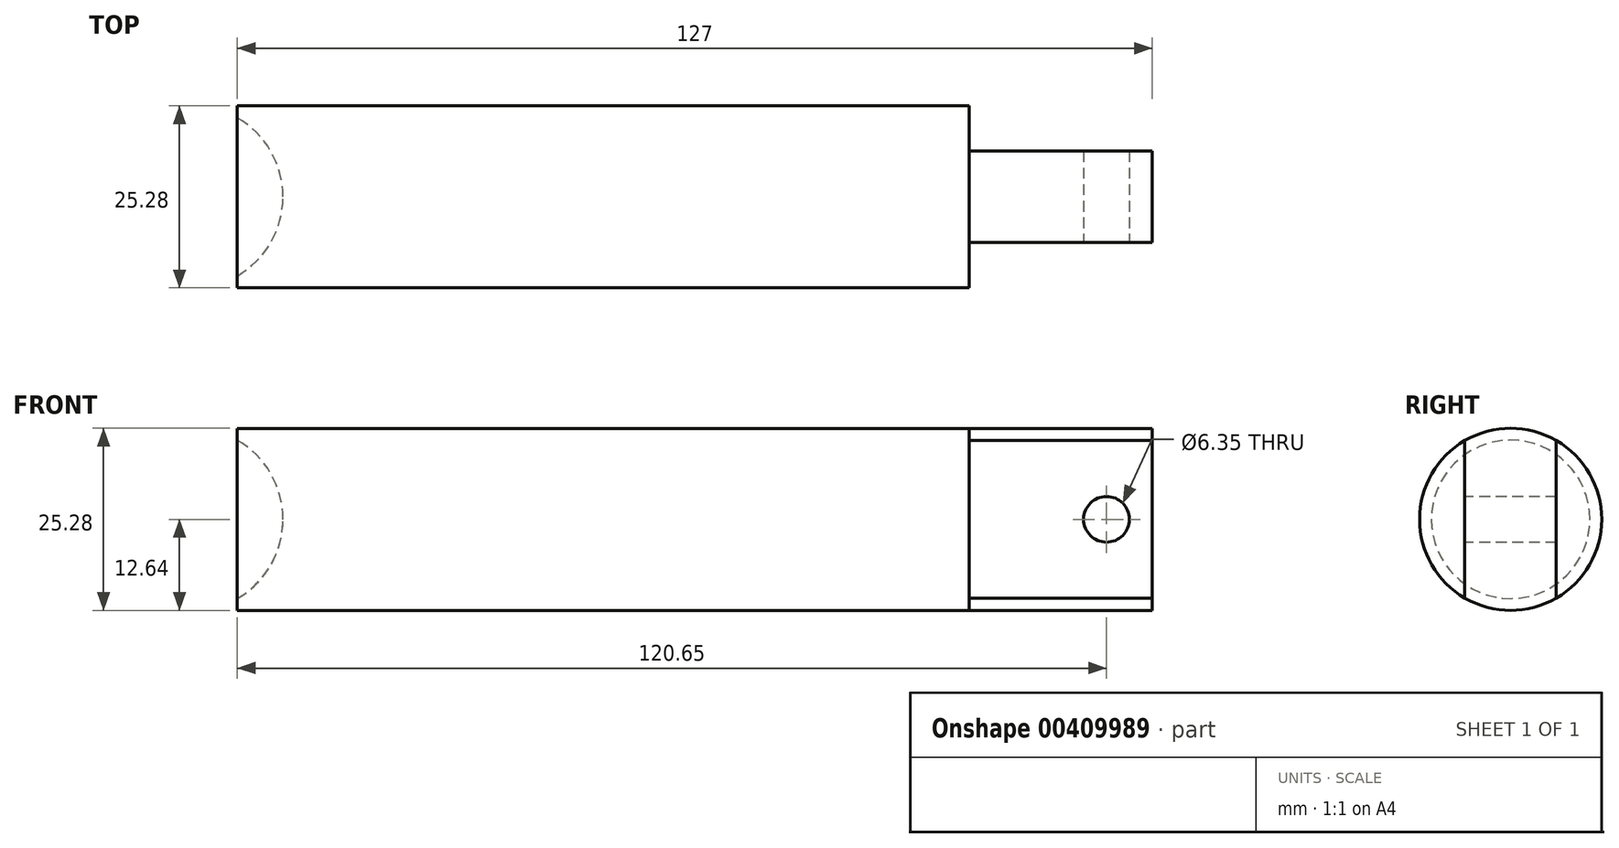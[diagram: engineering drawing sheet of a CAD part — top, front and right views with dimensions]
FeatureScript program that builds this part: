
annotation { "Feature Type Name" : "Feature", "Feature Type Description" : "" }
export const myFeature = defineFeature(function(context is Context, id is Id, definition is map)
    precondition{}
    {
        {
            var Q0;
            Q0=qCreatedBy(makeId("Front.planeOp"),FACE);
            var sketch = newSketch(context, id + "F0", { "sketchPlane" : qUnion([Q0])});
            skLineSegment(sketch, "E0.bottom", {"start": v(0, 12.64) * mm, "end": v(101.6, 12.64) * mm});
            skLineSegment(sketch, "E0.left", {"start": v(0, 12.64) * mm, "end": v(0, 0) * mm});
            skLineSegment(sketch, "E0.right", {"start": v(101.6, 12.64) * mm, "end": v(101.6, 0) * mm});
            skLineSegment(sketch, "E1", {"start": v(101.6, 0) * mm, "end": v(132.42, 0) * mm});
            skPoint(sketch, "E1.endSnap0", {"position": v(101.6, 0) * mm});
            skLineSegment(sketch, "E2", {"start": v(101.6, 0) * mm, "end": v(0, 0) * mm});
            skSolve(sketch);
        }
        {
            var Q0;
            {var subQ1=sQuery(id+"F0.wireOp",EDGE,"E0.bottom");Q0=makeQuery(id+"F0.imprint","IMPRINT",FACE,{"disambiguationData":[TD([[makeQuery(id+"F0.imprint","IMPRINT",EDGE,{"derivedFrom":subQ1}),-1.0]])]});}
            var Q1;
            Q1=sQuery(id+"F0.wireOp",EDGE,"E1");
            revolve(context, id + "F1", {"entities" : qUnion([Q0]), "axis" : qUnion([Q1]), "revolveType" : RevolveType.FULL});
        }
        {
            var Q0;
            Q0=qCreatedBy(makeId("Front.planeOp"),FACE);
            var sketch = newSketch(context, id + "F2", { "sketchPlane" : qUnion([Q0])});
            skArc(sketch, "E3", {"start": v(6.35, 0) * mm, "mid": v(4.65, 6.35) * mm, "end": v(0, 11) * mm});
            skLineSegment(sketch, "E4", {"start": v(0, 11) * mm, "end": v(0, 0) * mm});
            skLineSegment(sketch, "E5", {"start": v(0, 0) * mm, "end": v(6.35, 0) * mm});
            skSolve(sketch);
        }
        {
            var Q0;
            Q0 = qSketchRegion(id + "F2", true);
            var Q1;
            Q1=sQuery(id+"F2.wireOp",EDGE,"E5");
            revolve(context, id + "F3", {"operationType" : NewBodyOperationType.REMOVE, "entities" : qUnion([Q0]), "axis" : qUnion([Q1]), "revolveType" : RevolveType.FULL, "oppositeDirection" : true});
        }
        {
            var Q0;
            Q0=makeQuery(id+"F1.opRevolve","SWEPT_FACE",FACE,{"disambiguationData":[OSD([sQuery(id+"F0.wireOp",EDGE,"E0.right")])]});
            var sketch = newSketch(context, id + "F4", { "sketchPlane" : qUnion([Q0])});
            skLineSegment(sketch, "E6", {"start": v(-6.35, 10.93) * mm, "end": v(-6.35, -10.93) * mm});
            skLineSegment(sketch, "E7", {"start": v(6.35, 10.93) * mm, "end": v(6.35, -10.93) * mm});
            skArc(sketch, "E8", {"start": v(6.35, 10.93) * mm, "mid": v(0, 12.64) * mm, "end": v(-6.35, 10.93) * mm});
            skArc(sketch, "E9.trimOffspring", {"start": v(-6.35, -10.93) * mm, "mid": v(0, -12.64) * mm, "end": v(6.35, -10.93) * mm});
            skSolve(sketch);
        }
        {
            var Q0;
            Q0 = qSketchRegion(id + "F4", true);
            extrude(context, id + "F5", {"entities" : qUnion([Q0]), "depth" : 25.4 * mm});
        }
        {
            var Q0;
            Q0=makeQuery(id+"F5.opExtrude","SWEPT_FACE",FACE,{"disambiguationData":[OSD([sQuery(id+"F4.wireOp",EDGE,"E6")])]});
            var sketch = newSketch(context, id + "F6", { "sketchPlane" : qUnion([Q0])});
            skPoint(sketch, "E10", {"position": v(120.65, 0) * mm});
            skPoint(sketch, "E10.positionSnap0", {"position": v(127, 0) * mm});
            skSolve(sketch);
        }
        {
            var Q0;
            Q0=sQuery(id+"F6.wireOp",VERTEX,"E10");
            var Q1;
            Q1=makeQuery(id+"F5.opExtrude","SWEPT_BODY",BODY,{"disambiguationData":[OSD([sQuery(id+"F4.wireOp",EDGE,"E6"),sQuery(id+"F4.wireOp",EDGE,"E7"),sQuery(id+"F4.wireOp",EDGE,"E8"),sQuery(id+"F4.wireOp",EDGE,"E9.trimOffspring")])]});
            hole(context, id + "F7", {"style" : HoleStyle.SIMPLE, "endStyle" : HoleEndStyle.THROUGH, "holeDiameter" : 6.35 * mm, "isTappedThrough" : true, "tappedDepth" : 12.7 * mm, "tapClearance" : 3, "locations" : qUnion([Q0]), "scope" : qUnion([Q1])});
        }
    });
